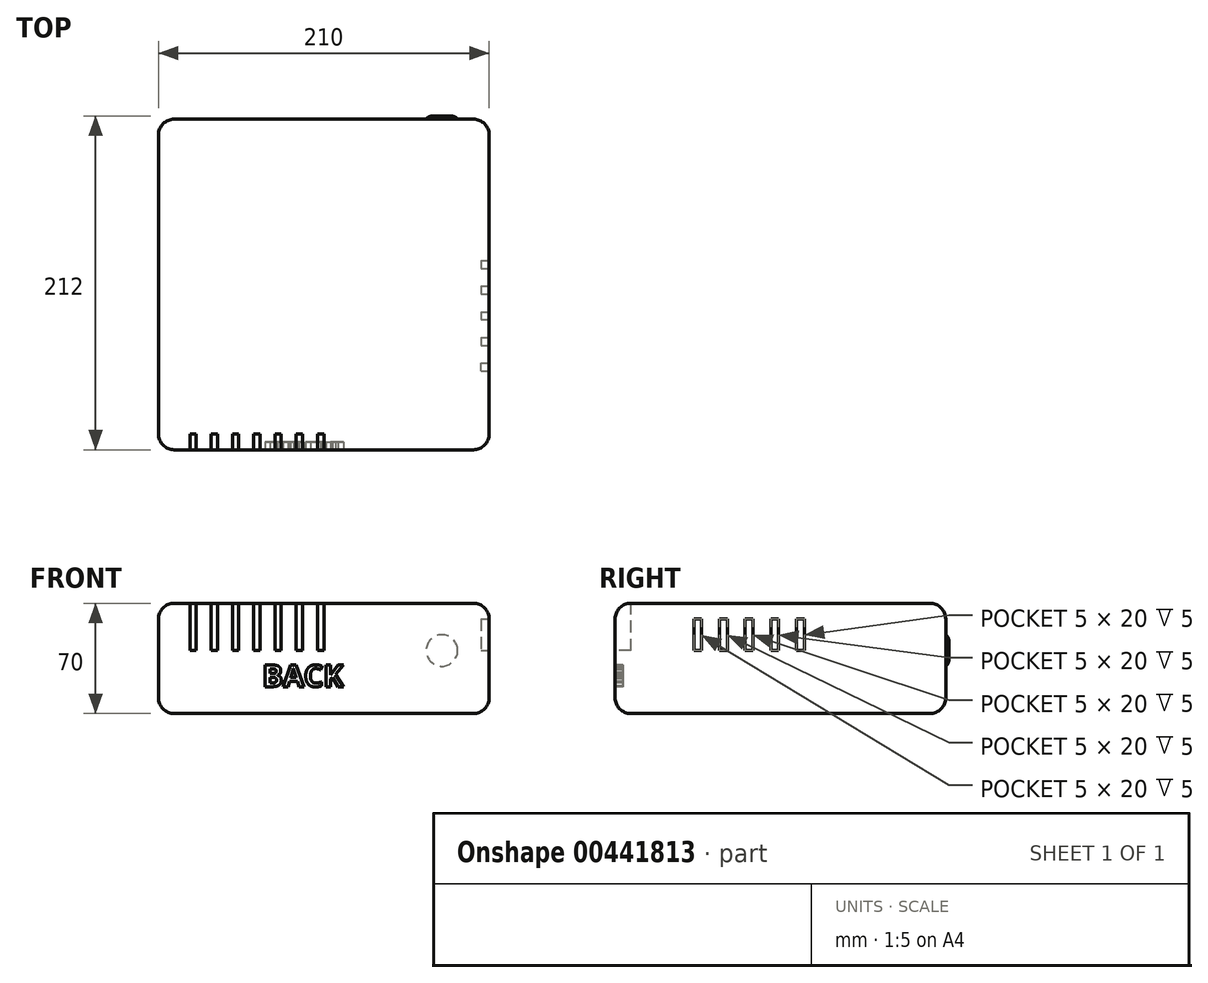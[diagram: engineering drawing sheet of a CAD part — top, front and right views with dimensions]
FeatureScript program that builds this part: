
annotation { "Feature Type Name" : "Feature", "Feature Type Description" : "" }
export const myFeature = defineFeature(function(context is Context, id is Id, definition is map)
    precondition{}
    {
        {
            var Q0;
            Q0=qCreatedBy(makeId("Top.planeOp"),FACE);
            var sketch = newSketch(context, id + "F0", { "sketchPlane" : qUnion([Q0])});
            skLineSegment(sketch, "E0.bottom", {"start": v(105, 105) * mm, "end": v(-105, 105) * mm});
            skLineSegment(sketch, "E0.top", {"start": v(105, -105) * mm, "end": v(-105, -105) * mm});
            skLineSegment(sketch, "E0.left", {"start": v(105, 105) * mm, "end": v(105, -105) * mm});
            skLineSegment(sketch, "E0.right", {"start": v(-105, 105) * mm, "end": v(-105, -105) * mm});
            skPoint(sketch, "E0.middle", {"position": v(0, 0) * mm});
            skSolve(sketch);
        }
        {
            var Q0;
            Q0=makeQuery(id+"F0.imprint","IMPRINT",FACE,{"disambiguationData":[TD([[makeQuery(id+"F0.imprint","IMPRINT",EDGE,{"derivedFrom":sQuery(id+"F0.wireOp",EDGE,"E0.bottom")}),1.0]])]});
            extrude(context, id + "F1", {"entities" : qUnion([Q0]), "depth" : 70 * mm});
        }
        {
            var Q0;
            Q0=makeQuery(id+"F1.opExtrude","SWEPT_EDGE",EDGE,{"disambiguationData":[OSD([sQuery(id+"F0.wireOp",EDGE,"E0.bottom"),sQuery(id+"F0.wireOp",EDGE,"E0.right")])]});
            var Q1;
            Q1=makeQuery(id+"F1.opExtrude","SWEPT_EDGE",EDGE,{"disambiguationData":[OSD([sQuery(id+"F0.wireOp",EDGE,"E0.bottom"),sQuery(id+"F0.wireOp",EDGE,"E0.left")])]});
            var Q2;
            Q2=makeQuery(id+"F1.opExtrude","SWEPT_EDGE",EDGE,{"disambiguationData":[OSD([sQuery(id+"F0.wireOp",EDGE,"E0.top"),sQuery(id+"F0.wireOp",EDGE,"E0.right")])]});
            var Q3;
            Q3=makeQuery(id+"F1.opExtrude","SWEPT_EDGE",EDGE,{"disambiguationData":[OSD([sQuery(id+"F0.wireOp",EDGE,"E0.top"),sQuery(id+"F0.wireOp",EDGE,"E0.left")])]});
            fillet(context, id + "F2", {"entities" : qUnion([Q0, Q1, Q2, Q3]), "radius" : 10 * mm, "tangentPropagation" : true, "allowEdgeOverflow" : false});
        }
        {
            var Q0;
            Q0=makeQuery(id+"F1.opExtrude","CAP_EDGE",EDGE,{"disambiguationData":[OSD([sQuery(id+"F0.wireOp",EDGE,"E0.left")])],"isStart":false});
            var Q1;
            Q1=makeQuery(id+"F1.opExtrude","CAP_EDGE",EDGE,{"disambiguationData":[OSD([sQuery(id+"F0.wireOp",EDGE,"E0.left")])],"isStart":true});
            fillet(context, id + "F3", {"entities" : qUnion([Q0, Q1]), "radius" : 10 * mm, "tangentPropagation" : true, "allowEdgeOverflow" : false});
        }
        {
            var Q0;
            Q0=makeQuery(id+"F1.opExtrude","SWEPT_FACE",FACE,{"disambiguationData":[OSD([sQuery(id+"F0.wireOp",EDGE,"E0.top")])]});
            var sketch = newSketch(context, id + "F4", { "sketchPlane" : qUnion([Q0])});
            skLineSegment(sketch, "E1.left", {"start": v(-85, 40) * mm, "end": v(-85, 70) * mm});
            skLineSegment(sketch, "E1.right", {"start": v(0, 40) * mm, "end": v(0, 70) * mm});
            skLineSegment(sketch, "E2.bottom", {"start": v(-85, 70) * mm, "end": v(-81, 70) * mm});
            skLineSegment(sketch, "E2.top", {"start": v(-85, 40) * mm, "end": v(-81, 40) * mm});
            skLineSegment(sketch, "E2.left", {"start": v(-85, 70) * mm, "end": v(-85, 40) * mm});
            skLineSegment(sketch, "E2.right", {"start": v(-81, 70) * mm, "end": v(-81, 40) * mm});
            skLineSegment(sketch, "E3.1.0.0", {"start": v(-71.5, 70) * mm, "end": v(-67.5, 70) * mm});
            skLineSegment(sketch, "E3.1.0.1", {"start": v(-71.5, 40) * mm, "end": v(-71.5, 70) * mm});
            skLineSegment(sketch, "E3.1.0.2", {"start": v(-67.5, 70) * mm, "end": v(-67.5, 40) * mm});
            skLineSegment(sketch, "E3.1.0.3", {"start": v(-71.5, 40) * mm, "end": v(-67.5, 40) * mm});
            skLineSegment(sketch, "E3.2.0.0", {"start": v(-58, 70) * mm, "end": v(-54, 70) * mm});
            skLineSegment(sketch, "E3.2.0.1", {"start": v(-58, 40) * mm, "end": v(-58, 70) * mm});
            skLineSegment(sketch, "E3.2.0.2", {"start": v(-54, 70) * mm, "end": v(-54, 40) * mm});
            skLineSegment(sketch, "E3.2.0.3", {"start": v(-58, 40) * mm, "end": v(-54, 40) * mm});
            skLineSegment(sketch, "E3.3.0.0", {"start": v(-44.5, 70) * mm, "end": v(-40.5, 70) * mm});
            skLineSegment(sketch, "E3.3.0.1", {"start": v(-44.5, 40) * mm, "end": v(-44.5, 70) * mm});
            skLineSegment(sketch, "E3.3.0.2", {"start": v(-40.5, 70) * mm, "end": v(-40.5, 40) * mm});
            skLineSegment(sketch, "E3.3.0.3", {"start": v(-44.5, 40) * mm, "end": v(-40.5, 40) * mm});
            skLineSegment(sketch, "E3.4.0.0", {"start": v(-31, 70) * mm, "end": v(-27, 70) * mm});
            skLineSegment(sketch, "E3.4.0.1", {"start": v(-31, 40) * mm, "end": v(-31, 70) * mm});
            skLineSegment(sketch, "E3.4.0.2", {"start": v(-27, 70) * mm, "end": v(-27, 40) * mm});
            skLineSegment(sketch, "E3.4.0.3", {"start": v(-31, 40) * mm, "end": v(-27, 40) * mm});
            skLineSegment(sketch, "E3.5.0.0", {"start": v(-17.5, 70) * mm, "end": v(-13.5, 70) * mm});
            skLineSegment(sketch, "E3.5.0.1", {"start": v(-17.5, 40) * mm, "end": v(-17.5, 70) * mm});
            skLineSegment(sketch, "E3.5.0.2", {"start": v(-13.5, 70) * mm, "end": v(-13.5, 40) * mm});
            skLineSegment(sketch, "E3.5.0.3", {"start": v(-17.5, 40) * mm, "end": v(-13.5, 40) * mm});
            skLineSegment(sketch, "E3.6.0.0", {"start": v(-4, 70) * mm, "end": v(0, 70) * mm});
            skLineSegment(sketch, "E3.6.0.1", {"start": v(-4, 40) * mm, "end": v(-4, 70) * mm});
            skLineSegment(sketch, "E3.6.0.2", {"start": v(0, 70) * mm, "end": v(0, 40) * mm});
            skLineSegment(sketch, "E3.6.0.3", {"start": v(-4, 40) * mm, "end": v(0, 40) * mm});
            skSolve(sketch);
        }
        {
            var Q0;
            Q0=qSketchRegion(id+"F4",true);
            extrude(context, id + "F5", {"entities" : qUnion([Q0]), "operationType" : NewBodyOperationType.REMOVE, "oppositeDirection" : true, "depth" : 10 * mm});
        }
        {
            var Q0;
            Q0=makeQuery(id+"F1.opExtrude","SWEPT_FACE",FACE,{"disambiguationData":[OSD([sQuery(id+"F0.wireOp",EDGE,"E0.left")])]});
            var sketch = newSketch(context, id + "F6", { "sketchPlane" : qUnion([Q0])});
            skLineSegment(sketch, "E4", {"start": v(-105, 60) * mm, "end": v(-55, 60) * mm, "construction": true});
            skLineSegment(sketch, "E5", {"start": v(-55, 60) * mm, "end": v(-55, 70) * mm, "construction": true});
            skLineSegment(sketch, "E6.left", {"start": v(-55, 60) * mm, "end": v(-55, 40) * mm, "construction": true});
            skLineSegment(sketch, "E6.right", {"start": v(15, 60) * mm, "end": v(15, 40) * mm, "construction": true});
            skLineSegment(sketch, "E7.bottom", {"start": v(-55, 40) * mm, "end": v(-50, 40) * mm});
            skLineSegment(sketch, "E7.top", {"start": v(-55, 60) * mm, "end": v(-50, 60) * mm});
            skLineSegment(sketch, "E7.left", {"start": v(-55, 40) * mm, "end": v(-55, 60) * mm});
            skLineSegment(sketch, "E7.right", {"start": v(-50, 40) * mm, "end": v(-50, 60) * mm});
            skLineSegment(sketch, "E8.1.0.0", {"start": v(-38.7, 60) * mm, "end": v(-33.7, 60) * mm});
            skLineSegment(sketch, "E8.1.0.1", {"start": v(-38.7, 60) * mm, "end": v(-38.7, 40) * mm});
            skLineSegment(sketch, "E8.1.0.2", {"start": v(-33.7, 40) * mm, "end": v(-33.7, 60) * mm});
            skLineSegment(sketch, "E8.1.0.3", {"start": v(-38.7, 40) * mm, "end": v(-33.7, 40) * mm});
            skLineSegment(sketch, "E8.2.0.0", {"start": v(-22.4, 60) * mm, "end": v(-17.4, 60) * mm});
            skLineSegment(sketch, "E8.2.0.1", {"start": v(-22.4, 60) * mm, "end": v(-22.4, 40) * mm});
            skLineSegment(sketch, "E8.2.0.2", {"start": v(-17.4, 40) * mm, "end": v(-17.4, 60) * mm});
            skLineSegment(sketch, "E8.2.0.3", {"start": v(-22.4, 40) * mm, "end": v(-17.4, 40) * mm});
            skLineSegment(sketch, "E8.3.0.0", {"start": v(-6.1, 60) * mm, "end": v(-1.1, 60) * mm});
            skLineSegment(sketch, "E8.3.0.1", {"start": v(-6.1, 60) * mm, "end": v(-6.1, 40) * mm});
            skLineSegment(sketch, "E8.3.0.2", {"start": v(-1.1, 40) * mm, "end": v(-1.1, 60) * mm});
            skLineSegment(sketch, "E8.3.0.3", {"start": v(-6.1, 40) * mm, "end": v(-1.1, 40) * mm});
            skLineSegment(sketch, "E8.4.0.0", {"start": v(10.2, 60) * mm, "end": v(15.2, 60) * mm});
            skLineSegment(sketch, "E8.4.0.1", {"start": v(10.2, 60) * mm, "end": v(10.2, 40) * mm});
            skLineSegment(sketch, "E8.4.0.2", {"start": v(15.2, 40) * mm, "end": v(15.2, 60) * mm});
            skLineSegment(sketch, "E8.4.0.3", {"start": v(10.2, 40) * mm, "end": v(15.2, 40) * mm});
            skLineSegment(sketch, "E8.direction1", {"start": v(-55, 60) * mm, "end": v(-38.7, 60) * mm, "construction": true});
            skSolve(sketch);
        }
        {
            var Q0;
            Q0=qSketchRegion(id+"F6",true);
            var Q1;
            Q1=sQuery(id+"F6.wireOp",EDGE,"E7.top");
            var Q2;
            Q2=sQuery(id+"F6.wireOp",EDGE,"E8.4.0.0");
            var Q3;
            Q3=sQuery(id+"F6.wireOp",EDGE,"E8.1.0.0");
            var Q4;
            Q4=sQuery(id+"F6.wireOp",EDGE,"E8.1.0.3");
            var Q5;
            Q5=sQuery(id+"F6.wireOp",EDGE,"E8.4.0.3");
            var Q6;
            Q6=sQuery(id+"F6.wireOp",EDGE,"E7.bottom");
            extrude(context, id + "F7", {"entities" : qUnion([Q0]), "operationType" : NewBodyOperationType.REMOVE, "surfaceEntities" : qUnion([Q1, Q2, Q3, Q4, Q5, Q6]), "oppositeDirection" : true, "depth" : 5 * mm});
        }
        {
            var Q0;
            Q0=makeQuery(id+"F1.opExtrude","SWEPT_FACE",FACE,{"disambiguationData":[OSD([sQuery(id+"F0.wireOp",EDGE,"E0.top")])]});
            var sketch = newSketch(context, id + "F8", { "sketchPlane" : qUnion([Q0])});
            skText(sketch, "E9", { "text": "BACK", "fontName": "OpenSans-Bold.ttf"});
            const initialGuessF8  = {"E9": [-0.03892, 0.01704, 1, 0, 0.01388]};
            skSetInitialGuess(sketch, initialGuessF8);
            skSolve(sketch);
        }
        {
            var Q0;
            Q0=qSketchRegion(id+"F8",true);
            extrude(context, id + "F9", {"entities" : qUnion([Q0]), "operationType" : NewBodyOperationType.REMOVE, "oppositeDirection" : true, "depth" : 5 * mm});
        }
        {
            var Q0;
            Q0=makeQuery(id+"F1.opExtrude","SWEPT_FACE",FACE,{"disambiguationData":[OSD([sQuery(id+"F0.wireOp",EDGE,"E0.bottom")])]});
            var sketch = newSketch(context, id + "F10", { "sketchPlane" : qUnion([Q0])});
            skCircle(sketch, "E10", {"center": v(-75, 40) * mm, "radius": 10 * mm});
            skSolve(sketch);
        }
        {
            var Q0;
            Q0 = qSketchRegion(id + "F10", true);
            extrude(context, id + "F11", {"entities" : qUnion([Q0]), "operationType" : NewBodyOperationType.ADD, "depth" : 2 * mm});
        }
        {
            var Q0;
            Q0=makeQuery(id+"F11.opExtrude","CAP_EDGE",EDGE,{"disambiguationData":[OSD([sQuery(id+"F10.wireOp",EDGE,"E10")])],"isStart":false});
            fillet(context, id + "F12", {"entities" : qUnion([Q0]), "radius" : 5 * mm, "tangentPropagation" : true, "allowEdgeOverflow" : false});
        }
    });
